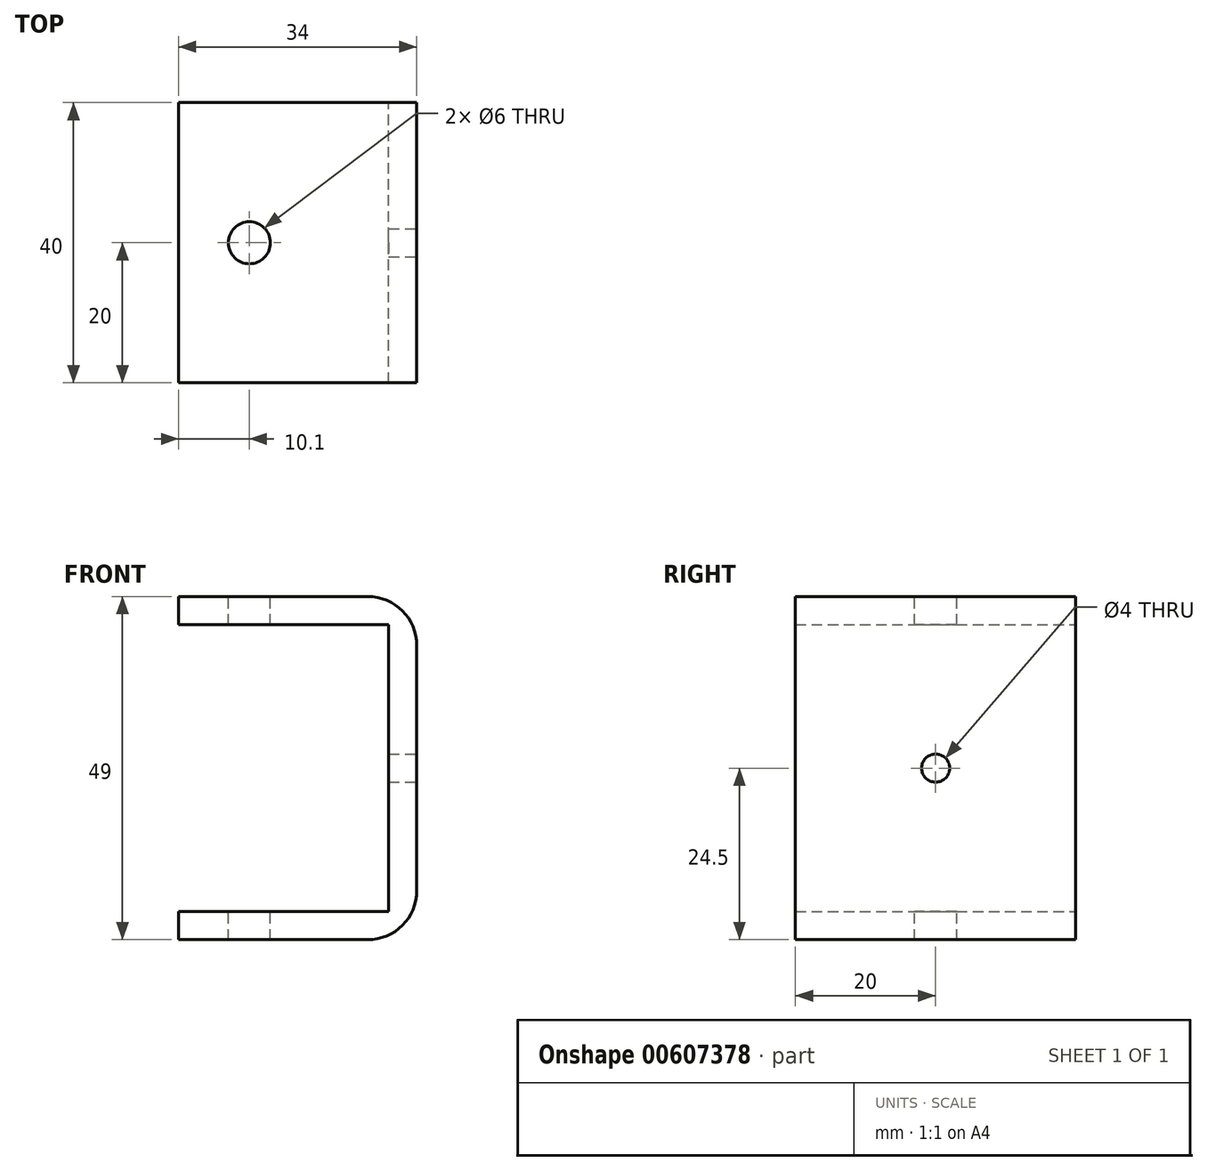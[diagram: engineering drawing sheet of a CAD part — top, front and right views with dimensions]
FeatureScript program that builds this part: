
annotation { "Feature Type Name" : "Feature", "Feature Type Description" : "" }
export const myFeature = defineFeature(function(context is Context, id is Id, definition is map)
    precondition{}
    {
        {
            var Q0;
            Q0=qCreatedBy(makeId("Front.planeOp"),FACE);
            var sketch = newSketch(context, id + "F0", { "sketchPlane" : qUnion([Q0])});
            skLineSegment(sketch, "E0.bottom", {"start": v(0, 0) * mm, "end": v(34, 0) * mm});
            skLineSegment(sketch, "E0.top", {"start": v(0, 49) * mm, "end": v(34, 49) * mm});
            skLineSegment(sketch, "E0.left", {"start": v(0, 0) * mm, "end": v(0, 49) * mm});
            skLineSegment(sketch, "E0.right", {"start": v(34, 0) * mm, "end": v(34, 49) * mm});
            skLineSegment(sketch, "E1.bottom", {"start": v(0, 4) * mm, "end": v(30, 4) * mm});
            skLineSegment(sketch, "E1.top", {"start": v(0, 45) * mm, "end": v(30, 45) * mm});
            skLineSegment(sketch, "E1.left", {"start": v(0, 4) * mm, "end": v(0, 45) * mm});
            skLineSegment(sketch, "E1.right", {"start": v(30, 4) * mm, "end": v(30, 45) * mm});
            skSolve(sketch);
        }
        {
            var Q0;
            {var subQ4=sQuery(id+"F0.wireOp",EDGE,"E0.bottom");Q0=makeQuery(id+"F0.imprint","IMPRINT",FACE,{"disambiguationData":[TD([[makeQuery(id+"F0.imprint","IMPRINT",EDGE,{"derivedFrom":subQ4}),1.0]])]});}
            extrude(context, id + "F1", {"entities" : qUnion([Q0]), "depth" : 20 * mm, "offsetDistance" : 25 * mm, "hasSecondDirection" : true, "secondDirectionOppositeDirection" : true, "secondDirectionDepth" : 20 * mm});
        }
        {
            var Q0;
            Q0=makeQuery(id+"F1.opExtrude","SWEPT_EDGE",EDGE,{"disambiguationData":[OSD([sQuery(id+"F0.wireOp",EDGE,"E0.top"),sQuery(id+"F0.wireOp",EDGE,"E0.right")])]});
            var Q1;
            Q1=makeQuery(id+"F1.opExtrude","SWEPT_EDGE",EDGE,{"disambiguationData":[OSD([sQuery(id+"F0.wireOp",EDGE,"E0.bottom"),sQuery(id+"F0.wireOp",EDGE,"E0.right")])]});
            fillet(context, id + "F2", {"entities" : qUnion([Q0, Q1]), "radius" : 7 * mm, "tangentPropagation" : true, "allowEdgeOverflow" : false});
        }
        {
            var Q0;
            Q0=makeQuery(id+"F1.opExtrude","SWEPT_FACE",FACE,{"disambiguationData":[OSD([sQuery(id+"F0.wireOp",EDGE,"E0.right")])]});
            var sketch = newSketch(context, id + "F3", { "sketchPlane" : qUnion([Q0])});
            skCircle(sketch, "E2", {"center": v(0, 24.5) * mm, "radius": 2 * mm});
            skLineSegment(sketch, "E3", {"start": v(0, 7) * mm, "end": v(0, 42) * mm, "construction": true});
            skSolve(sketch);
        }
        {
            var Q0;
            Q0=makeQuery(id+"F3.imprint","IMPRINT",FACE,{"disambiguationData":[TD([[makeQuery(id+"F3.imprint","IMPRINT",EDGE,{"derivedFrom":sQuery(id+"F3.wireOp",EDGE,"E2")}),1.0]])]});
            extrude(context, id + "F4", {"entities" : qUnion([Q0]), "operationType" : NewBodyOperationType.REMOVE, "oppositeDirection" : true, "depth" : 25 * mm, "offsetDistance" : 25 * mm});
        }
        {
            var Q0;
            Q0=makeQuery(id+"F1.opExtrude","SWEPT_FACE",FACE,{"disambiguationData":[OSD([sQuery(id+"F0.wireOp",EDGE,"E0.top")])]});
            var sketch = newSketch(context, id + "F5", { "sketchPlane" : qUnion([Q0])});
            skCircle(sketch, "E4", {"center": v(10.1, 0) * mm, "radius": 3 * mm});
            skSolve(sketch);
        }
        {
            var Q0;
            Q0=makeQuery(id+"F5.imprint","IMPRINT",FACE,{"disambiguationData":[TD([[makeQuery(id+"F5.imprint","IMPRINT",EDGE,{"derivedFrom":sQuery(id+"F5.wireOp",EDGE,"E4")}),1.0]])]});
            extrude(context, id + "F6", {"entities" : qUnion([Q0]), "operationType" : NewBodyOperationType.REMOVE, "oppositeDirection" : true, "depth" : 53 * mm, "offsetDistance" : 25 * mm});
        }
    });
